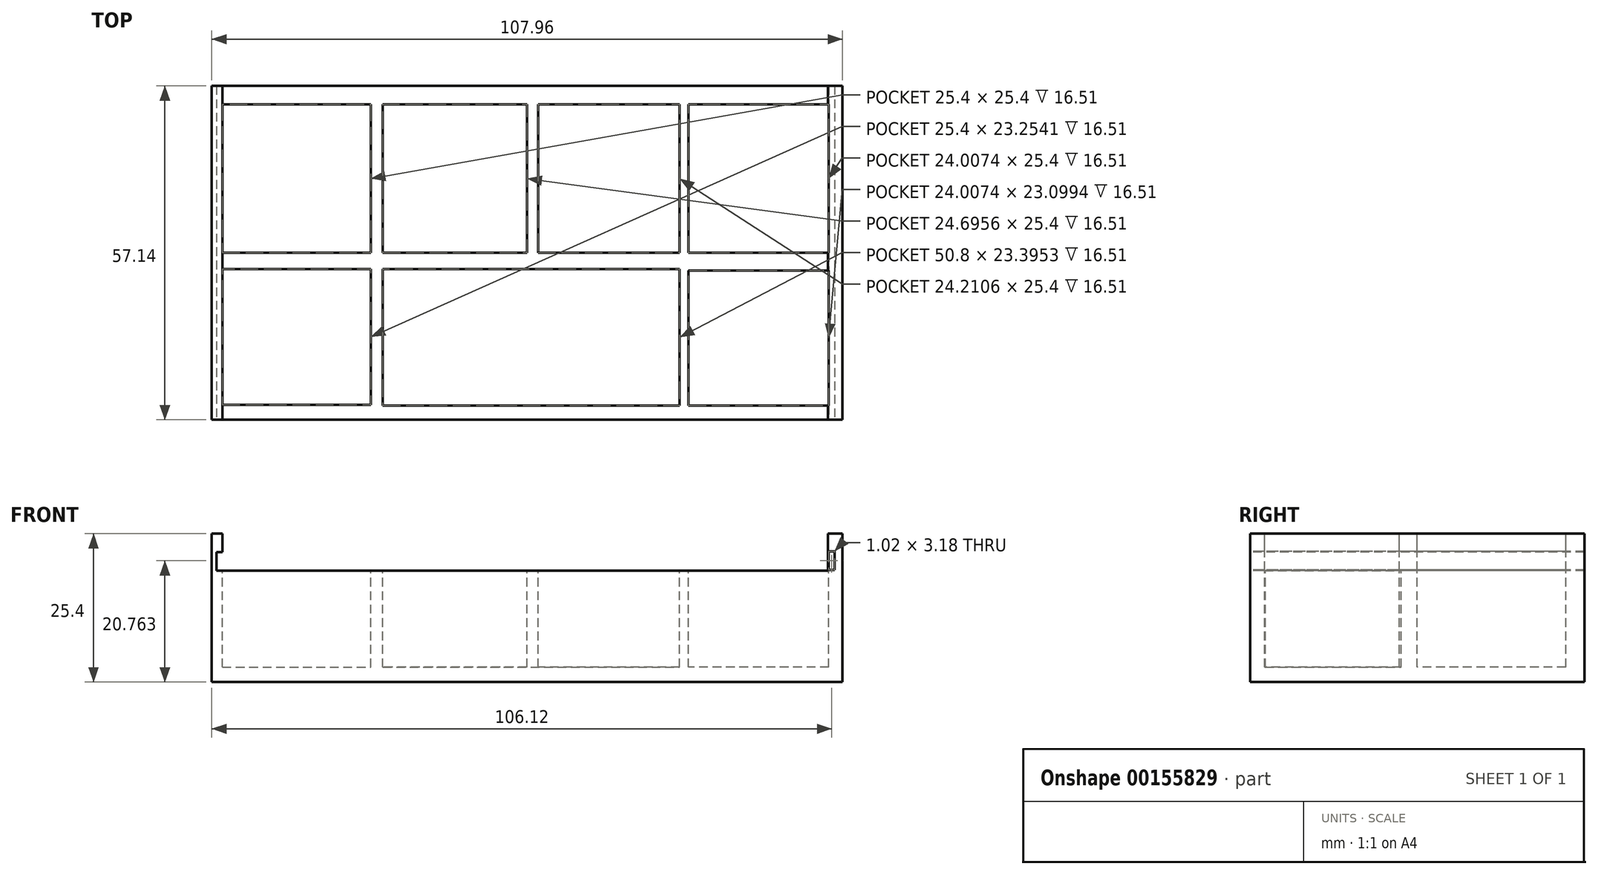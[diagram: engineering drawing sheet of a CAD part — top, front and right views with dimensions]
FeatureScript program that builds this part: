
annotation { "Feature Type Name" : "Feature", "Feature Type Description" : "" }
export const myFeature = defineFeature(function(context is Context, id is Id, definition is map)
    precondition{}
    {
        {
            var Q0;
            Q0=qCreatedBy(makeId("Top.planeOp"),FACE);
            var sketch = newSketch(context, id + "F0", { "sketchPlane" : qUnion([Q0])});
            skLineSegment(sketch, "E0.bottom", {"start": v(53.98, -28.57) * mm, "end": v(-53.98, -28.58) * mm});
            skLineSegment(sketch, "E0.top", {"start": v(53.98, 28.58) * mm, "end": v(-53.98, 28.57) * mm});
            skLineSegment(sketch, "E0.left", {"start": v(53.98, -28.57) * mm, "end": v(53.98, 28.58) * mm});
            skLineSegment(sketch, "E0.right", {"start": v(-53.98, -28.58) * mm, "end": v(-53.98, 28.57) * mm});
            skPoint(sketch, "E0.middle", {"position": v(0, 0) * mm});
            skSolve(sketch);
        }
        {
            var Q0;
            Q0 = qSketchRegion(id + "F0", true);
            extrude(context, id + "F1", {"entities" : qUnion([Q0]), "depth" : 25.4 * mm});
        }
        {
            var Q0;
            Q0=makeQuery(id+"F1.opExtrude","CAP_FACE",FACE,{"disambiguationData":[OSD([sQuery(id+"F0.wireOp",EDGE,"E0.bottom"),sQuery(id+"F0.wireOp",EDGE,"E0.top"),sQuery(id+"F0.wireOp",EDGE,"E0.left"),sQuery(id+"F0.wireOp",EDGE,"E0.right")])],"isStart":false});
            var sketch = newSketch(context, id + "F2", { "sketchPlane" : qUnion([Q0])});
            skLineSegment(sketch, "E1.bottom", {"start": v(-52.16, 25.4) * mm, "end": v(-26.76, 25.4) * mm});
            skLineSegment(sketch, "E1.top", {"start": v(-52.16, 0) * mm, "end": v(-26.76, 0) * mm});
            skLineSegment(sketch, "E1.left", {"start": v(-52.16, 25.4) * mm, "end": v(-52.16, 0) * mm});
            skLineSegment(sketch, "E1.right", {"start": v(-26.76, 25.4) * mm, "end": v(-26.76, 0) * mm});
            skLineSegment(sketch, "E2.bottom", {"start": v(-52.16, -26.01) * mm, "end": v(-26.76, -26.01) * mm});
            skLineSegment(sketch, "E2.top", {"start": v(-52.16, -2.76) * mm, "end": v(-26.76, -2.76) * mm});
            skLineSegment(sketch, "E2.left", {"start": v(-52.16, -26.01) * mm, "end": v(-52.16, -2.76) * mm});
            skLineSegment(sketch, "E2.right", {"start": v(-26.76, -26.01) * mm, "end": v(-26.76, -2.76) * mm});
            skLineSegment(sketch, "E3.bottom", {"start": v(0, 25.4) * mm, "end": v(-24.7, 25.4) * mm});
            skLineSegment(sketch, "E3.top", {"start": v(0, 0) * mm, "end": v(-24.7, 0) * mm});
            skLineSegment(sketch, "E3.left", {"start": v(0, 25.4) * mm, "end": v(0, 0) * mm});
            skLineSegment(sketch, "E3.right", {"start": v(-24.7, 25.4) * mm, "end": v(-24.7, 0) * mm});
            skLineSegment(sketch, "E4.bottom", {"start": v(-24.7, -2.76) * mm, "end": v(26.1, -2.76) * mm});
            skLineSegment(sketch, "E4.top", {"start": v(-24.7, -26.15) * mm, "end": v(26.1, -26.15) * mm});
            skLineSegment(sketch, "E4.left", {"start": v(-24.7, -2.76) * mm, "end": v(-24.7, -26.15) * mm});
            skLineSegment(sketch, "E4.right", {"start": v(26.1, -2.76) * mm, "end": v(26.1, -26.15) * mm});
            skLineSegment(sketch, "E5.bottom", {"start": v(26.1, 25.4) * mm, "end": v(1.9, 25.4) * mm});
            skLineSegment(sketch, "E5.top", {"start": v(26.1, 0) * mm, "end": v(1.9, 0) * mm});
            skLineSegment(sketch, "E5.left", {"start": v(26.1, 25.4) * mm, "end": v(26.1, 0) * mm});
            skLineSegment(sketch, "E5.right", {"start": v(1.9, 25.4) * mm, "end": v(1.9, 0) * mm});
            skLineSegment(sketch, "E6.bottom", {"start": v(51.63, 25.4) * mm, "end": v(27.63, 25.4) * mm});
            skLineSegment(sketch, "E6.top", {"start": v(51.63, 0) * mm, "end": v(27.63, 0) * mm});
            skLineSegment(sketch, "E6.left", {"start": v(51.63, 25.4) * mm, "end": v(51.63, 0) * mm});
            skLineSegment(sketch, "E6.right", {"start": v(27.63, 25.4) * mm, "end": v(27.63, 0) * mm});
            skLineSegment(sketch, "E7.bottom", {"start": v(51.63, -26.15) * mm, "end": v(27.63, -26.15) * mm});
            skLineSegment(sketch, "E7.top", {"start": v(51.63, -3.06) * mm, "end": v(27.63, -3.06) * mm});
            skLineSegment(sketch, "E7.left", {"start": v(51.63, -26.15) * mm, "end": v(51.63, -3.06) * mm});
            skLineSegment(sketch, "E7.right", {"start": v(27.63, -26.15) * mm, "end": v(27.63, -3.06) * mm});
            skSolve(sketch);
        }
        {
            var Q0;
            Q0 = qSketchRegion(id + "F2", true);
            extrude(context, id + "F3", {"entities" : qUnion([Q0]), "operationType" : NewBodyOperationType.REMOVE, "oppositeDirection" : true, "depth" : 22.86 * mm});
        }
        {
            var Q0;
            Q0=makeQuery(id+"F1.opExtrude","CAP_FACE",FACE,{"disambiguationData":[OSD([sQuery(id+"F0.wireOp",EDGE,"E0.bottom"),sQuery(id+"F0.wireOp",EDGE,"E0.top"),sQuery(id+"F0.wireOp",EDGE,"E0.left"),sQuery(id+"F0.wireOp",EDGE,"E0.right")])],"isStart":false});
            var sketch = newSketch(context, id + "F4", { "sketchPlane" : qUnion([Q0])});
            skLineSegment(sketch, "E8.bottom", {"start": v(-52.16, 28.57) * mm, "end": v(51.5, 28.57) * mm});
            skLineSegment(sketch, "E8.top", {"start": v(-52.16, -28.57) * mm, "end": v(51.5, -28.57) * mm});
            skLineSegment(sketch, "E8.left", {"start": v(-52.16, 28.57) * mm, "end": v(-52.16, -28.57) * mm});
            skLineSegment(sketch, "E8.right", {"start": v(51.5, 28.57) * mm, "end": v(51.5, -28.57) * mm});
            skSolve(sketch);
        }
        {
            var Q0;
            Q0 = qSketchRegion(id + "F4", true);
            extrude(context, id + "F5", {"entities" : qUnion([Q0]), "operationType" : NewBodyOperationType.REMOVE, "oppositeDirection" : true, "depth" : 6.35 * mm});
        }
        {
            var Q0;
            Q0=makeQuery(id+"F5.boolean.opBoolean","MERGE",FACE,{"derivedFrom":[makeQuery(id+"F3.boolean.opBoolean","COPY",FACE,{"derivedFrom":makeQuery(id+"F3.opExtrude","SWEPT_FACE",FACE,{"disambiguationData":[OSD([sQuery(id+"F2.wireOp",EDGE,"E1.left")])]})}),makeQuery(id+"F3.boolean.opBoolean","COPY",FACE,{"derivedFrom":makeQuery(id+"F3.opExtrude","SWEPT_FACE",FACE,{"disambiguationData":[OSD([sQuery(id+"F2.wireOp",EDGE,"E2.left")])]})}),makeQuery(id+"F5.opExtrude","SWEPT_FACE",FACE,{"disambiguationData":[OSD([sQuery(id+"F4.wireOp",EDGE,"E8.left")])]})]});
            var sketch = newSketch(context, id + "F6", { "sketchPlane" : qUnion([Q0])});
            skLineSegment(sketch, "E9.bottom", {"start": v(28.57, 19.05) * mm, "end": v(-28.58, 19.05) * mm});
            skLineSegment(sketch, "E9.top", {"start": v(28.57, 22.22) * mm, "end": v(-28.58, 22.22) * mm});
            skLineSegment(sketch, "E9.left", {"start": v(28.57, 19.05) * mm, "end": v(28.57, 22.22) * mm});
            skLineSegment(sketch, "E9.right", {"start": v(-28.58, 19.05) * mm, "end": v(-28.58, 22.22) * mm});
            skSolve(sketch);
        }
        {
            var Q0;
            Q0 = qSketchRegion(id + "F6", true);
            extrude(context, id + "F7", {"entities" : qUnion([Q0]), "operationType" : NewBodyOperationType.REMOVE, "oppositeDirection" : true, "depth" : 1.02 * mm});
        }
        {
            var Q0;
            Q0=makeQuery(id+"F3.boolean.opBoolean","COPY",FACE,{"derivedFrom":makeQuery(id+"F3.opExtrude","SWEPT_FACE",FACE,{"disambiguationData":[OSD([sQuery(id+"F2.wireOp",EDGE,"E6.left")])]})});
            var sketch = newSketch(context, id + "F8", { "sketchPlane" : qUnion([Q0])});
            skLineSegment(sketch, "E10.bottom", {"start": v(-28.54, 19.18) * mm, "end": v(28.6, 19.18) * mm});
            skLineSegment(sketch, "E10.top", {"start": v(-28.54, 22.35) * mm, "end": v(28.6, 22.35) * mm});
            skLineSegment(sketch, "E10.left", {"start": v(-28.54, 19.18) * mm, "end": v(-28.54, 22.35) * mm});
            skLineSegment(sketch, "E10.right", {"start": v(28.6, 19.18) * mm, "end": v(28.6, 22.35) * mm});
            skSolve(sketch);
        }
        {
            var Q0;
            Q0 = qSketchRegion(id + "F8", true);
            extrude(context, id + "F9", {"entities" : qUnion([Q0]), "operationType" : NewBodyOperationType.REMOVE, "oppositeDirection" : true, "depth" : 1.02 * mm});
        }
        {
            var Q0;
            Q0=makeQuery(id+"F9.boolean.opBoolean","COPY",FACE,{"derivedFrom":makeQuery(id+"F9.opExtrude","SWEPT_FACE",FACE,{"disambiguationData":[OSD([sQuery(id+"F8.wireOp",EDGE,"E10.left")])]})});
            extrude(context, id + "F10", {"entities" : qUnion([Q0]), "operationType" : NewBodyOperationType.REMOVE, "oppositeDirection" : true, "depth" : 57.15 * mm});
        }
    });
